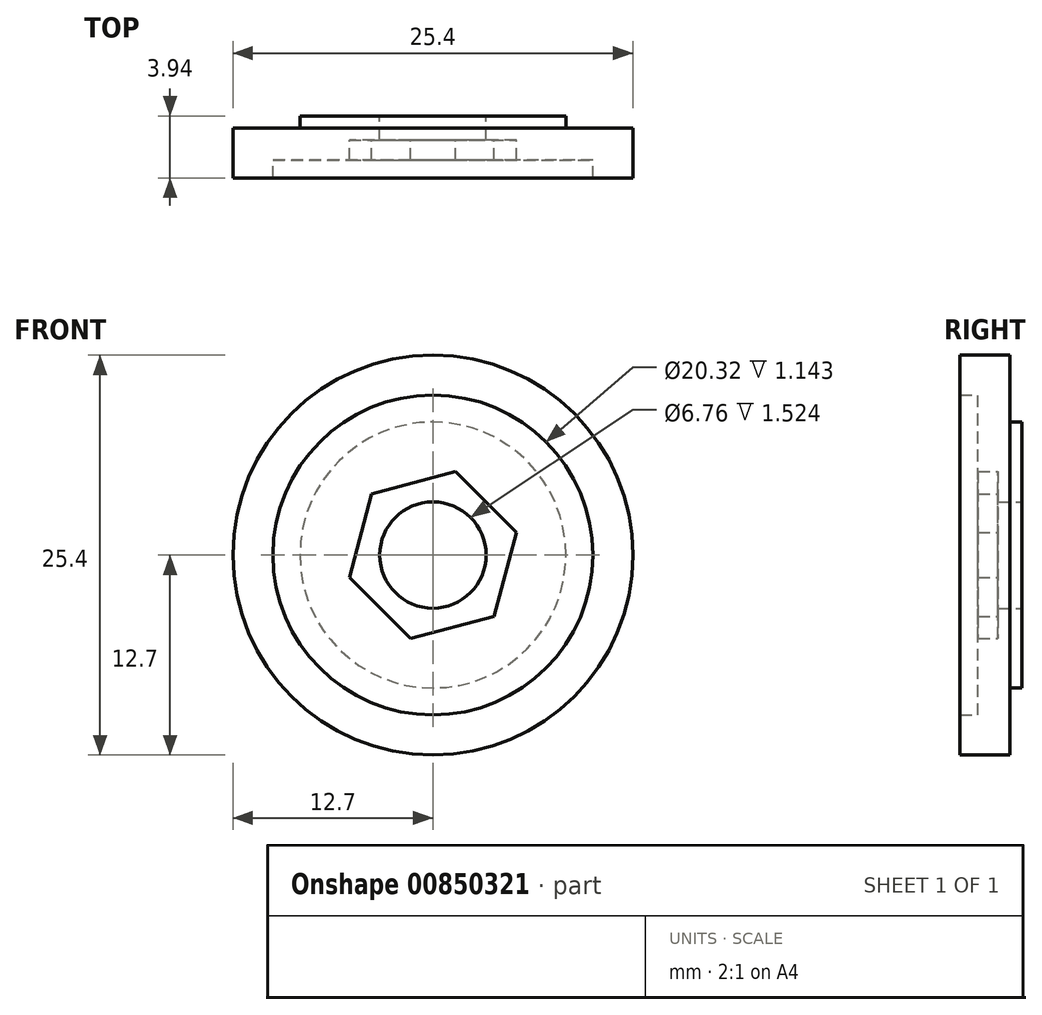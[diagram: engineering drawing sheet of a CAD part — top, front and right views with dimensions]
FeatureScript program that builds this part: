
annotation { "Feature Type Name" : "Feature", "Feature Type Description" : "" }
export const myFeature = defineFeature(function(context is Context, id is Id, definition is map)
    precondition{}
    {
        {
            var Q0;
            Q0=qCreatedBy(makeId("Front.planeOp"),FACE);
            var sketch = newSketch(context, id + "F0", { "sketchPlane" : qUnion([Q0])});
            skCircle(sketch, "E0", {"center": v(0, 0) * mm, "radius": 3.38 * mm});
            skCircle(sketch, "E1", {"center": v(0, 0) * mm, "radius": 10.16 * mm});
            skCircle(sketch, "E2", {"center": v(0, 0) * mm, "radius": 12.7 * mm});
            skCircle(sketch, "E3.cCircle", {"center": v(0, 0) * mm, "radius": 4.76 * mm, "construction": true});
            skLineSegment(sketch, "E3.0", {"start": v(5.31, 1.42) * mm, "end": v(3.89, -3.89) * mm});
            skLineSegment(sketch, "E3.1", {"start": v(3.89, -3.89) * mm, "end": v(-1.42, -5.31) * mm});
            skLineSegment(sketch, "E3.2", {"start": v(-1.42, -5.31) * mm, "end": v(-5.31, -1.42) * mm});
            skLineSegment(sketch, "E3.3", {"start": v(-5.31, -1.42) * mm, "end": v(-3.89, 3.89) * mm});
            skLineSegment(sketch, "E3.4", {"start": v(-3.89, 3.89) * mm, "end": v(1.42, 5.31) * mm});
            skLineSegment(sketch, "E3.5", {"start": v(1.42, 5.31) * mm, "end": v(5.31, 1.42) * mm});
            skPoint(sketch, "E3.0.midPoint", {"position": v(4.6, -1.23) * mm});
            skSolve(sketch);
        }
        {
            var Q0;
            Q0=makeQuery(id+"F0.imprint","IMPRINT",FACE,{"disambiguationData":[TD([[makeQuery(id+"F0.imprint","IMPRINT",EDGE,{"derivedFrom":sQuery(id+"F0.wireOp",EDGE,"E1")}),-1.0]])]});
            var Q1;
            Q1=sQuery(id+"F0.wireOp",EDGE,"E2");
            extrude(context, id + "F1", {"entities" : qUnion([Q0]), "surfaceEntities" : qUnion([Q1]), "depth" : 3.17 * mm, "offsetDistance" : 25.4 * mm});
        }
        {
            var Q0;
            Q0=makeQuery(id+"F0.imprint","IMPRINT",FACE,{"disambiguationData":[TD([[makeQuery(id+"F0.imprint","IMPRINT",EDGE,{"derivedFrom":sQuery(id+"F0.wireOp",EDGE,"E1")}),1.0]])]});
            var Q1;
            Q1=sQuery(id+"F0.wireOp",EDGE,"E1");
            extrude(context, id + "F2", {"entities" : qUnion([Q0]), "operationType" : NewBodyOperationType.ADD, "surfaceEntities" : qUnion([Q1]), "depth" : 2.03 * mm, "offsetDistance" : 25.4 * mm});
        }
        {
            var Q0;
            Q0=makeQuery(id+"F0.imprint","IMPRINT",FACE,{"disambiguationData":[TD([[makeQuery(id+"F0.imprint","IMPRINT",EDGE,{"derivedFrom":sQuery(id+"F0.wireOp",EDGE,"E0")}),-1.0]])]});
            extrude(context, id + "F3", {"entities" : qUnion([Q0]), "operationType" : NewBodyOperationType.ADD, "depth" : 0.76 * mm, "offsetDistance" : 25.4 * mm});
        }
        {
            var Q0;
            Q0=makeQuery(id+"F0.imprint","IMPRINT",FACE,{"disambiguationData":[TD([[makeQuery(id+"F0.imprint","IMPRINT",EDGE,{"derivedFrom":sQuery(id+"F0.wireOp",EDGE,"E0")}),1.0]])]});
            var sketch = newSketch(context, id + "F4", { "sketchPlane" : qUnion([Q0])});
            skCircle(sketch, "E4", {"center": v(0, 0) * mm, "radius": 8.45 * mm});
            skSolve(sketch);
        }
        {
            var Q0;
            Q0 = qSketchRegion(id + "F4", true);
            extrude(context, id + "F5", {"entities" : qUnion([Q0]), "operationType" : NewBodyOperationType.ADD, "oppositeDirection" : true, "depth" : 0.76 * mm, "offsetDistance" : 25.4 * mm});
        }
        {
            var Q0;
            Q0=makeQuery(id+"F0.imprint","IMPRINT",FACE,{"disambiguationData":[TD([[makeQuery(id+"F0.imprint","IMPRINT",EDGE,{"derivedFrom":sQuery(id+"F0.wireOp",EDGE,"E0")}),1.0]])]});
            var Q1;
            Q1=sQuery(id+"F0.wireOp",EDGE,"E0");
            extrude(context, id + "F6", {"entities" : qUnion([Q0]), "bodyType" : ToolBodyType.SURFACE, "surfaceEntities" : qUnion([Q1]), "oppositeDirection" : true, "depth" : 0.76 * mm, "offsetDistance" : 25.4 * mm, "hasSecondDirection" : true, "secondDirectionOppositeDirection" : false, "secondDirectionDepth" : 0.25 * mm});
        }
        {
            var Q0;
            Q0=sQuery(id+"F0.wireOp",VERTEX,"E0.center");
            var Q1;
            Q1=makeQuery(id+"F1.opExtrude","SWEPT_BODY",BODY,{"disambiguationData":[OSD([sQuery(id+"F0.wireOp",EDGE,"E1"),sQuery(id+"F0.wireOp",EDGE,"E2")])]});
            hole(context, id + "F7", {"style" : HoleStyle.SIMPLE, "endStyle" : HoleEndStyle.THROUGH, "holeDiameter" : 6.76 * mm, "majorDiameter" : 6.35 * mm, "isTappedThrough" : true, "tappedDepth" : 12.7 * mm, "tapClearance" : 3, "locations" : qUnion([Q0]), "scope" : qUnion([Q1])});
        }
    });
